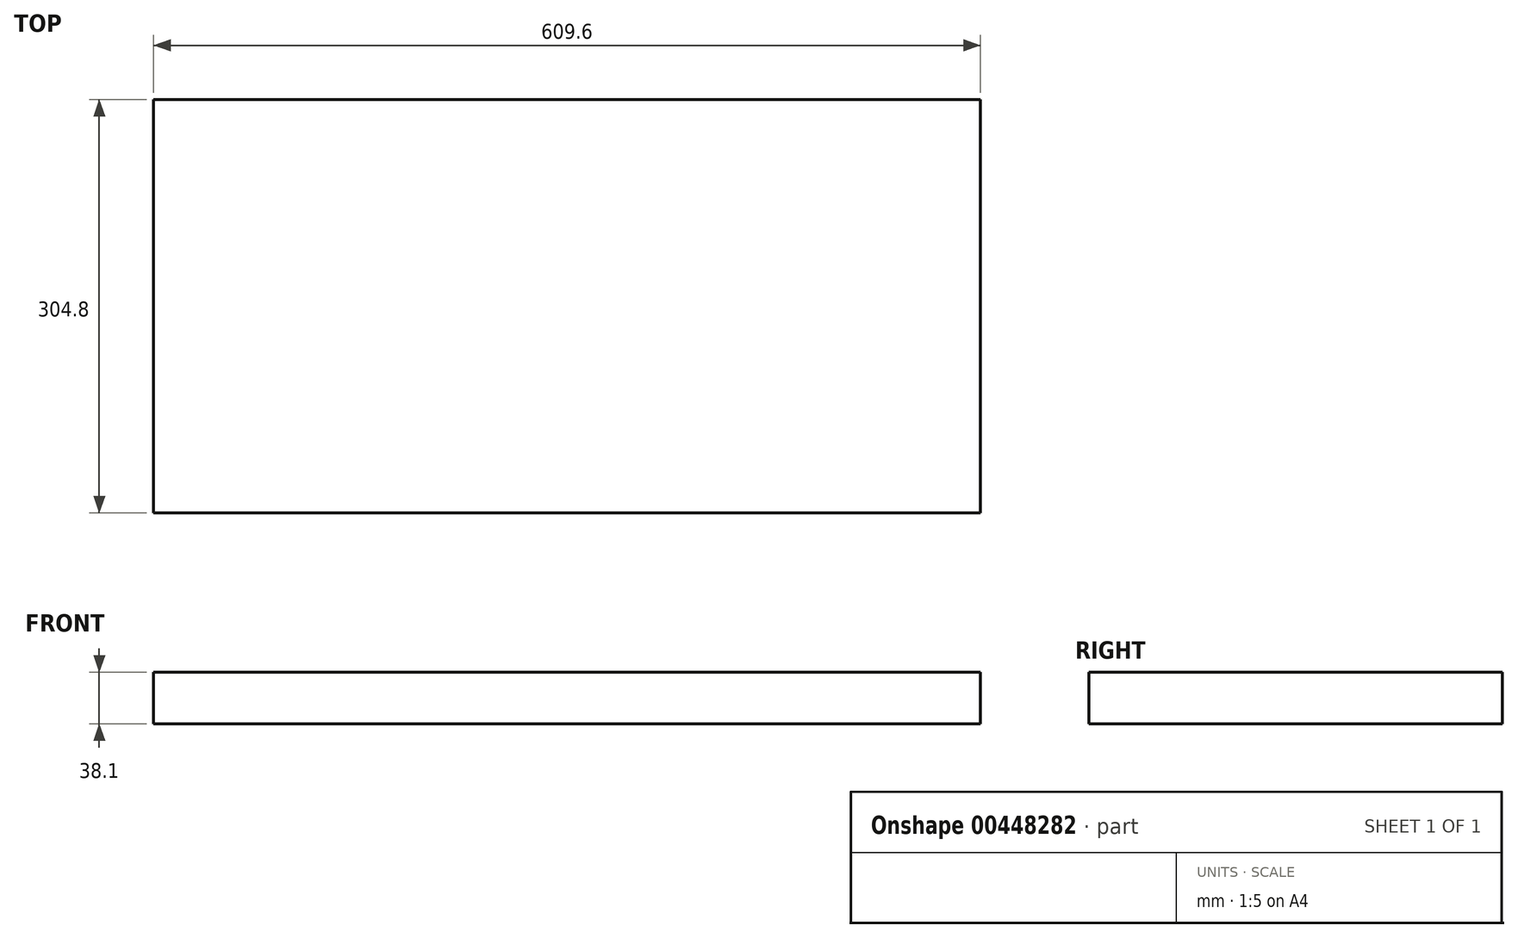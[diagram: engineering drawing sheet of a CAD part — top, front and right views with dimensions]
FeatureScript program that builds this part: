
annotation { "Feature Type Name" : "Feature", "Feature Type Description" : "" }
export const myFeature = defineFeature(function(context is Context, id is Id, definition is map)
    precondition{}
    {
        {
            var Q0;
            Q0=qCreatedBy(makeId("Right.planeOp"),FACE);
            var sketch = newSketch(context, id + "F0", { "sketchPlane" : qUnion([Q0])});
            skLineSegment(sketch, "E0.bottom", {"start": v(-304.8, 38.1) * mm, "end": v(0, 38.1) * mm});
            skLineSegment(sketch, "E0.top", {"start": v(-304.8, 0) * mm, "end": v(0, 0) * mm});
            skLineSegment(sketch, "E0.left", {"start": v(-304.8, 38.1) * mm, "end": v(-304.8, 0) * mm});
            skLineSegment(sketch, "E0.right", {"start": v(0, 38.1) * mm, "end": v(0, 0) * mm});
            skSolve(sketch);
        }
        {
            var Q0;
            Q0=makeQuery(id+"F0.imprint","IMPRINT",FACE,{"disambiguationData":[TD([[makeQuery(id+"F0.imprint","IMPRINT",EDGE,{"derivedFrom":sQuery(id+"F0.wireOp",EDGE,"E0.bottom")}),-1.0]])]});
            extrude(context, id + "F1", {"entities" : qUnion([Q0]), "oppositeDirection" : true, "depth" : 609.6 * mm});
        }
    });
